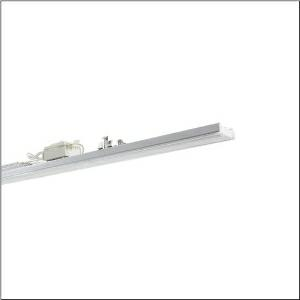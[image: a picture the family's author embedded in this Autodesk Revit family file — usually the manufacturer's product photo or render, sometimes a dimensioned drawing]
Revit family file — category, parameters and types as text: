
# Revit family: licross_r__11_recessed_ho_51tl1edv4m1s_bf61
name_source: partatom
category: Lighting Fixtures
units: mm (PartAtom-declared; Revit-internal decimal feet)

## family parameters
Cut with Voids When Loaded = No
Host = Face
Light Source = No
Part Type = Normal
Room Calculation Point = No
Round Connector Dimension = Use Diameter
Shared = No

## types (1)
- --- (1 x LED, 26450 lm, 150.5 W, 4000K)
    Apparent Load = 150 VA
    CIE Flux Codes = 85 95 99 100 100
    Color Rendering = 80
    Color Temperature = 4000K
    Default Elevation = 1800 mm
    Description = Licross® 11 Recessed HO, luminaire insert, of sheet steel, coil coated, white, length: 2.250mm, width: 66mm, height: 67mm, LED rated luminous flux: 26.450lm, light colour: 840, control gear: DALI 2, with plug, 5-pole, with phase selection, mains connection: 220..240V, AC, 50/60Hz, rated input power: 151W, internal wiring halogen-free, primary light control with lens, of plastic, primary optical cover: cover, of PMMA, light emission: direct distribution, primary light characteristic: symmetric, protection rating (complete): IP40, insulation class (complete): insulation class I (protective earthing), certification: CE, ENEC, VDE, UKCA, protection symbol: D if used in an environment without relevant dust loads with corresponding accessories, impact resistance: IK06, permissible ambient temperature for indoor applications: -40..+35°C, corresponds to IFS (International Featured Standards) requirements for safety and quality in the food industry, reducing of maximum allowable ambient temperature of 5°C with ceiling mounting, LABS conformity tested according to VDMA 24364:2018-05, packaging unit: 1 piece
    Height = 58 mm
    Lamp = 1 x LED
    Lamp Light Flux = 26450 lm
    Lamp Power = 150.5 W
    Lamp count = 1
    Length = 2250 mm
    Luminous efficacy = 176 lm/W
    Manufacturer = Siteco
    ModVariant = No
    Model = 51TL1EDV4M1S
    Mounting Place = Ceiling
    Mounting Type = Pendant
    Number of Poles = 1
    OnlyDefault = Yes
    Power Factor = 1
    Product Name = Licross® 11 Recessed HO
    Product group = luminaire insert | ceiling pendant
    ProductGroupID = 902
    Protection Class = Protection class I
    Protection Degree = IP 40
    RLX_Detail_Level = 1
    RLX_Emergency_Light_Flux = 0 lm
    RLX_Emergency_Type = 0
    RLX_Emergency_Type_DB = No
    RlxData = <blob elided: 29541 chars, md5=f85bd47f>
    Socket = socket
    Standby Power = 0 W
    System Light Flux = 26450 lm
    System Power = 150 W
    Type Comments = factory setting: luminous flux: 100 % | dim-lin: 254 | 690 mA
    Type Image = l_1296930.jpg
    URL = http://relux.com
    VarID = @adj_117353
    Voltage = 0 V
    Weight = 0.00 kg
    Width = 66 mm

## geometry (parser evidence)
native form markers: Blend x4, Sweep x10
no freeform markers — native parametric forms only
